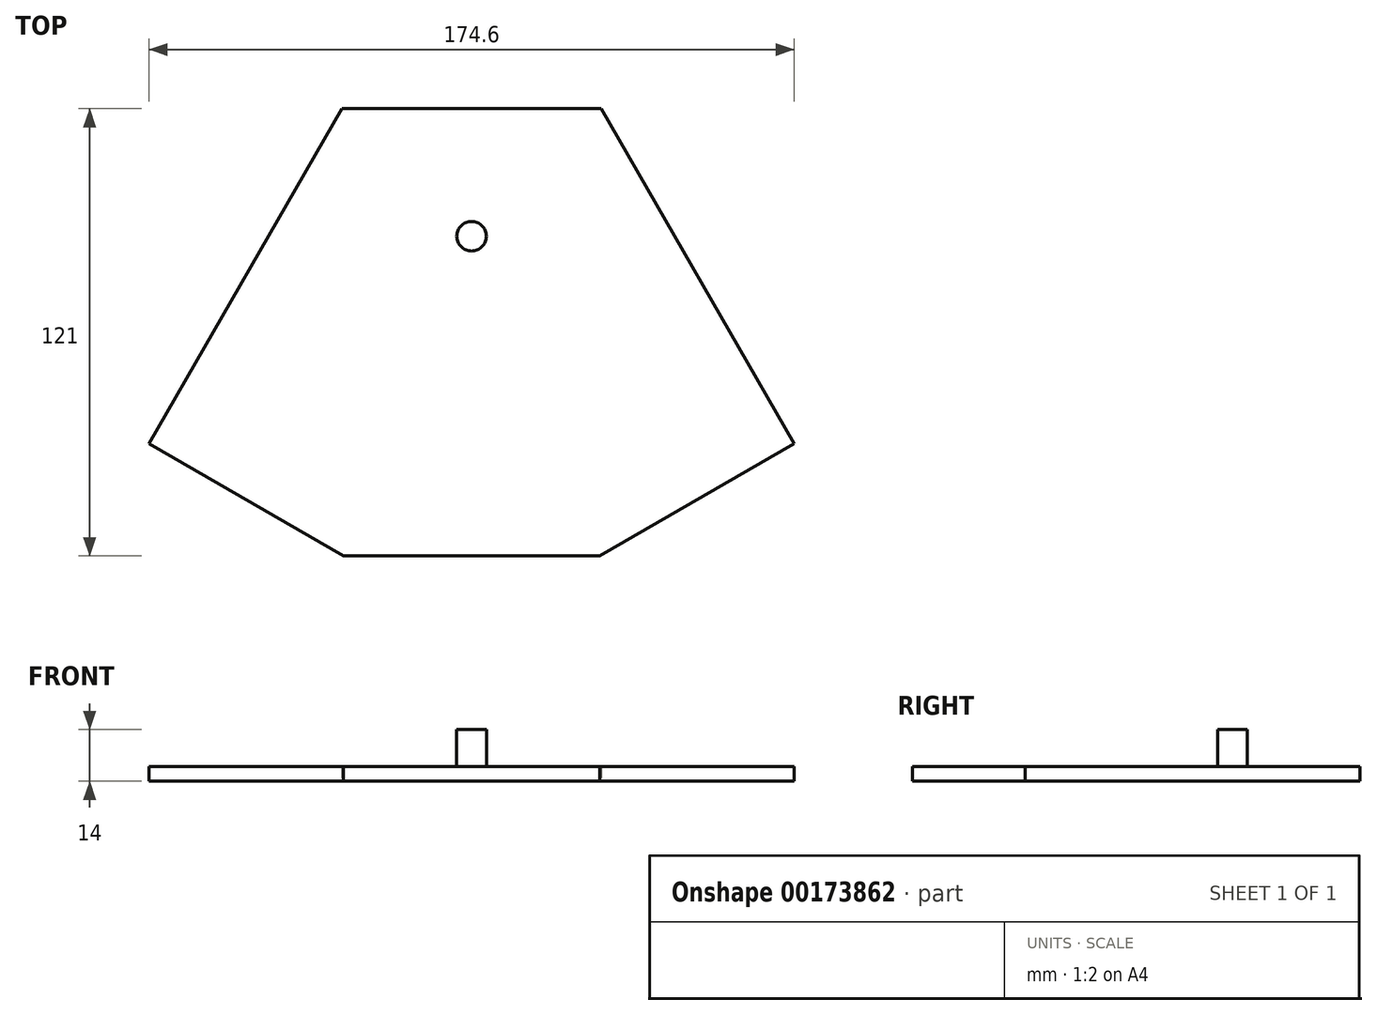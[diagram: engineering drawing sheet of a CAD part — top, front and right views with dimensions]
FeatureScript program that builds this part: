
annotation { "Feature Type Name" : "Feature", "Feature Type Description" : "" }
export const myFeature = defineFeature(function(context is Context, id is Id, definition is map)
    precondition{}
    {
        {
            var Q0;
            Q0=qCreatedBy(makeId("Top.planeOp"),FACE);
            var sketch = newSketch(context, id + "F0", { "sketchPlane" : qUnion([Q0])});
            skLineSegment(sketch, "E0", {"start": v(0, 0) * mm, "end": v(-35, 0) * mm});
            skLineSegment(sketch, "E1", {"start": v(0, 0) * mm, "end": v(35, 0) * mm});
            skLineSegment(sketch, "E2", {"start": v(-35, 0) * mm, "end": v(-87.3, -90.6) * mm});
            skLineSegment(sketch, "E3", {"start": v(-87.3, -90.6) * mm, "end": v(0, -141) * mm});
            skLineSegment(sketch, "E4", {"start": v(0, -141) * mm, "end": v(87.3, -90.6) * mm});
            skLineSegment(sketch, "E5", {"start": v(87.3, -90.6) * mm, "end": v(35, 0) * mm});
            skLineSegment(sketch, "E6", {"start": v(-34.64, -121) * mm, "end": v(34.64, -121) * mm});
            skSolve(sketch);
        }
        {
            var Q0;
            Q0=makeQuery(id+"F0.imprint","IMPRINT",FACE,{"disambiguationData":[TD([[makeQuery(id+"F0.imprint","IMPRINT",EDGE,{"derivedFrom":sQuery(id+"F0.wireOp",EDGE,"E0")}),1.0]])]});
            extrude(context, id + "F1", {"entities" : qUnion([Q0]), "depth" : 4 * mm});
        }
        {
            var Q0;
            Q0=makeQuery(id+"F1.opExtrude","CAP_FACE",FACE,{"disambiguationData":[OSD([sQuery(id+"F0.wireOp",EDGE,"E0"),sQuery(id+"F0.wireOp",EDGE,"E1"),sQuery(id+"F0.wireOp",EDGE,"E2"),sQuery(id+"F0.wireOp",EDGE,"E3"),sQuery(id+"F0.wireOp",EDGE,"E4"),sQuery(id+"F0.wireOp",EDGE,"E5")])],"isStart":false});
            var sketch = newSketch(context, id + "F2", { "sketchPlane" : qUnion([Q0])});
            skCircle(sketch, "E7", {"center": v(0, -34.5) * mm, "radius": 4 * mm});
            skLineSegment(sketch, "E8", {"start": v(0, 0) * mm, "end": v(0, -34.5) * mm});
            skPoint(sketch, "E8.endSnap0", {"position": v(0, 0) * mm});
            skSolve(sketch);
        }
        {
            var Q0;
            Q0=makeQuery(id+"F2.imprint","IMPRINT",FACE,{"disambiguationData":[TD([[makeQuery(id+"F2.imprint","IMPRINT",EDGE,{"derivedFrom":sQuery(id+"F2.wireOp",EDGE,"E7")}),1.0]])]});
            extrude(context, id + "F3", {"entities" : qUnion([Q0]), "operationType" : NewBodyOperationType.ADD, "depth" : 10 * mm});
        }
    });
